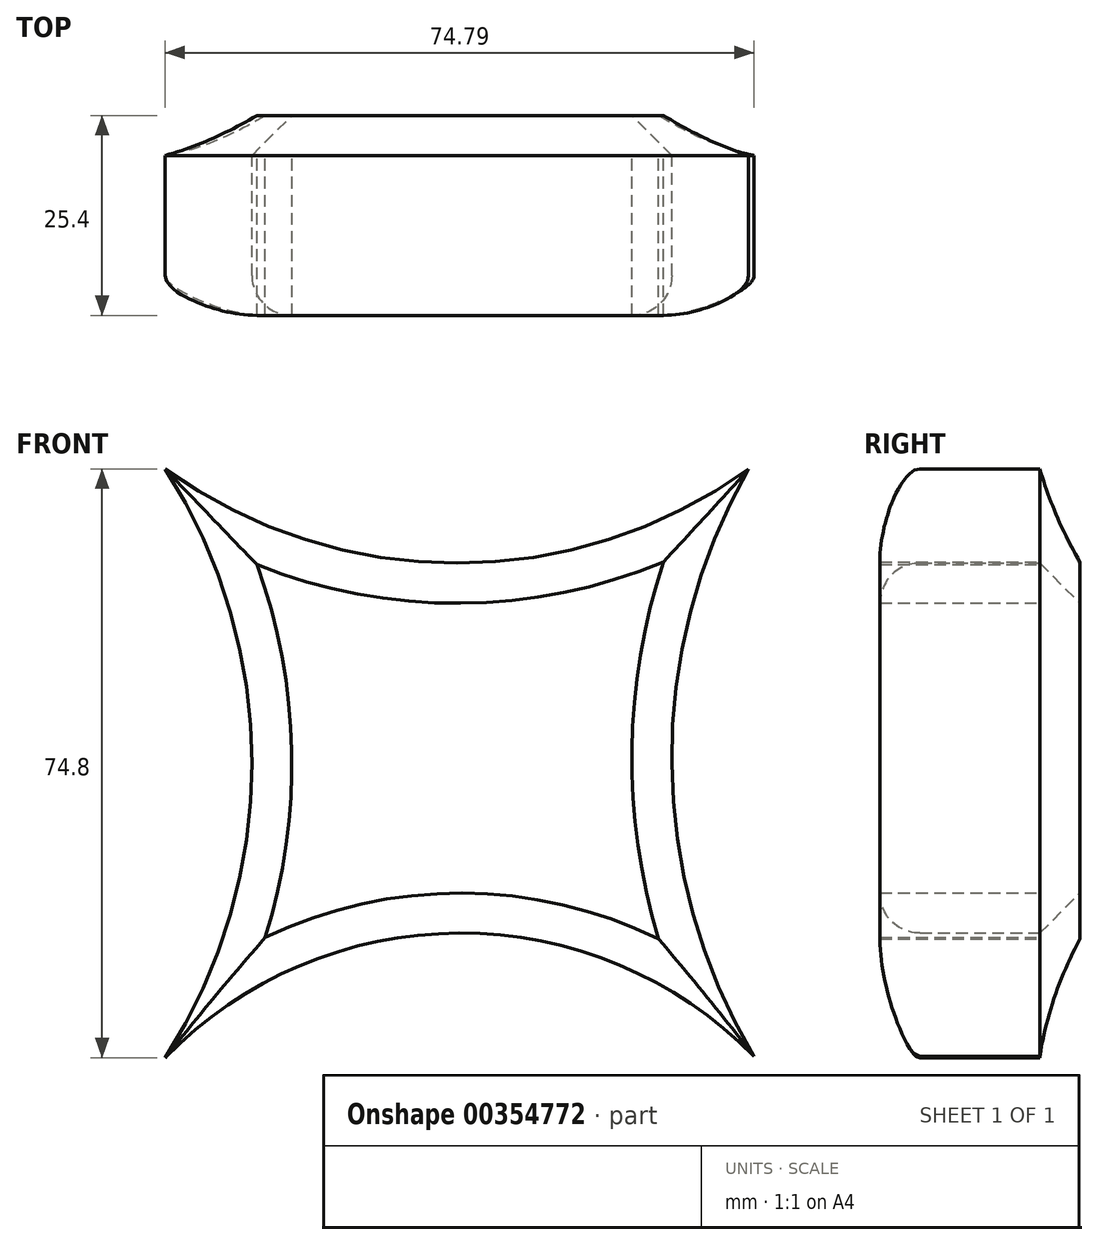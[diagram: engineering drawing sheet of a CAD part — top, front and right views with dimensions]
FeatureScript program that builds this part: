
annotation { "Feature Type Name" : "Feature", "Feature Type Description" : "" }
export const myFeature = defineFeature(function(context is Context, id is Id, definition is map)
    precondition{}
    {
        {
            var Q0;
            Q0=qCreatedBy(makeId("Front.planeOp"),FACE);
            var sketch = newSketch(context, id + "F0", { "sketchPlane" : qUnion([Q0])});
            skArc(sketch, "E0", {"start": v(-36.9, -37.38) * mm, "mid": v(-25.88, 0.02) * mm, "end": v(-36.9, 37.42) * mm});
            skArc(sketch, "E1", {"start": v(37.22, 37.42) * mm, "mid": v(27.46, 0.02) * mm, "end": v(37.89, -37.2) * mm});
            skArc(sketch, "E2", {"start": v(37.89, -37.2) * mm, "mid": v(0.46, -21.56) * mm, "end": v(-36.9, -37.38) * mm});
            skArc(sketch, "E3", {"start": v(-36.9, 37.42) * mm, "mid": v(0.16, 25.43) * mm, "end": v(37.22, 37.42) * mm});
            skLineSegment(sketch, "E4", {"start": v(0, 25.43) * mm, "end": v(0, -21.56) * mm});
            skLineSegment(sketch, "E5", {"start": v(-25.88, 0.02) * mm, "end": v(27.46, 0.02) * mm});
            skSolve(sketch);
        }
        {
            var Q0;
            Q0 = qSketchRegion(id + "F0", true);
            extrude(context, id + "F1", {"entities" : qUnion([Q0]), "endBound" : BoundingType.SYMMETRIC, "depth" : 25.4 * mm});
        }
        {
            var Q0;
            Q0=makeQuery(id+"F1.opExtrude","CAP_EDGE",EDGE,{"disambiguationData":[OSD([sQuery(id+"F0.wireOp",EDGE,"E3")])],"isStart":false});
            var Q1;
            Q1=makeQuery(id+"F1.opExtrude","CAP_EDGE",EDGE,{"disambiguationData":[OSD([sQuery(id+"F0.wireOp",EDGE,"E0")])],"isStart":false});
            var Q2;
            Q2=makeQuery(id+"F1.opExtrude","CAP_EDGE",EDGE,{"disambiguationData":[OSD([sQuery(id+"F0.wireOp",EDGE,"E1")])],"isStart":false});
            var Q3;
            Q3=makeQuery(id+"F1.opExtrude","CAP_EDGE",EDGE,{"disambiguationData":[OSD([sQuery(id+"F0.wireOp",EDGE,"E2")])],"isStart":false});
            fillet(context, id + "F2", {"entities" : qUnion([Q0, Q1, Q2, Q3]), "radius" : 5.08 * mm, "tangentPropagation" : true, "allowEdgeOverflow" : false});
        }
        {
            var Q0;
            Q0=makeQuery(id+"F1.opExtrude","CAP_FACE",FACE,{"disambiguationData":[OSD([sQuery(id+"F0.wireOp",EDGE,"E0"),sQuery(id+"F0.wireOp",EDGE,"E1"),sQuery(id+"F0.wireOp",EDGE,"E2"),sQuery(id+"F0.wireOp",EDGE,"E3")])],"isStart":false});
            shell(context, id + "F3", {"entities" : qUnion([Q0]), "thickness" : 5.08 * mm});
        }
        {
            var Q0;
            Q0=makeQuery(id+"F1.opExtrude","CAP_EDGE",EDGE,{"disambiguationData":[OSD([sQuery(id+"F0.wireOp",EDGE,"E3")])],"isStart":true});
            var Q1;
            Q1=makeQuery(id+"F1.opExtrude","CAP_EDGE",EDGE,{"disambiguationData":[OSD([sQuery(id+"F0.wireOp",EDGE,"E0")])],"isStart":true});
            var Q2;
            Q2=makeQuery(id+"F1.opExtrude","CAP_EDGE",EDGE,{"disambiguationData":[OSD([sQuery(id+"F0.wireOp",EDGE,"E1")])],"isStart":true});
            var Q3;
            Q3=makeQuery(id+"F1.opExtrude","CAP_EDGE",EDGE,{"disambiguationData":[OSD([sQuery(id+"F0.wireOp",EDGE,"E2")])],"isStart":true});
            chamfer(context, id + "F4", {"entities" : qUnion([Q0, Q1, Q2, Q3]), "width" : 5.08 * mm, "tangentPropagation" : true});
        }
    });
